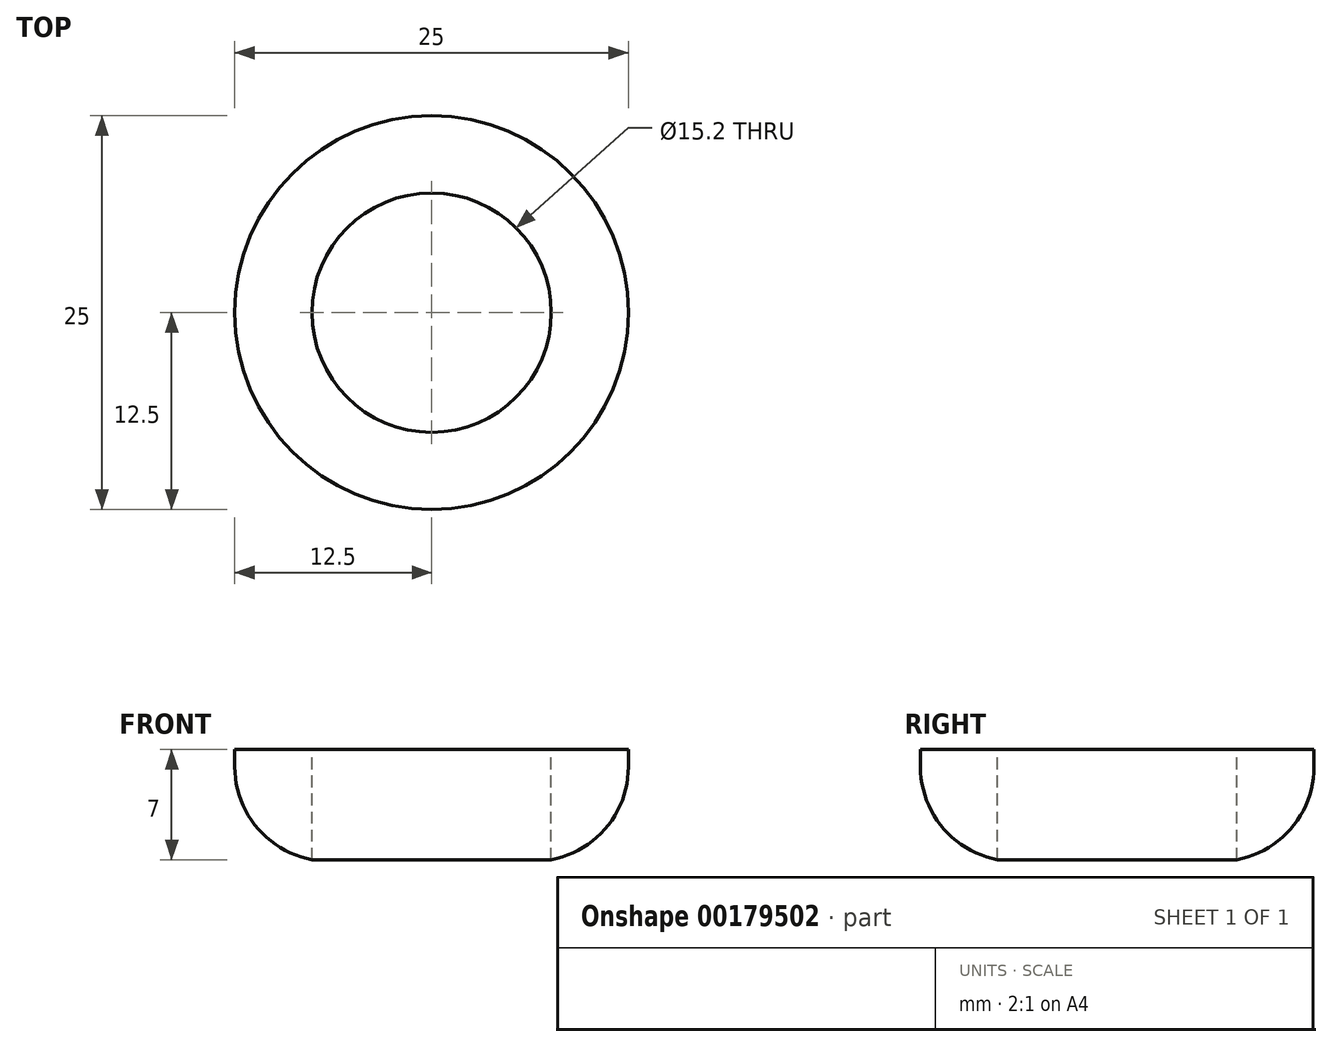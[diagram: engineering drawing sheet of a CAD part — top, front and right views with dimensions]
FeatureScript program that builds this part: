
annotation { "Feature Type Name" : "Feature", "Feature Type Description" : "" }
export const myFeature = defineFeature(function(context is Context, id is Id, definition is map)
    precondition{}
    {
        {
            var Q0;
            Q0=qCreatedBy(makeId("Top.planeOp"),FACE);
            var sketch = newSketch(context, id + "F0", { "sketchPlane" : qUnion([Q0])});
            skCircle(sketch, "E0", {"center": v(0, 0) * mm, "radius": 12.5 * mm});
            skCircle(sketch, "E1", {"center": v(0, 0) * mm, "radius": 7.6 * mm});
            skSolve(sketch);
        }
        {
            var Q0;
            Q0=qSketchRegion(id+"F0",true);
            extrude(context, id + "F1", {"entities" : qUnion([Q0]), "oppositeDirection" : true, "depth" : 7 * mm});
        }
        {
            var Q0;
            Q0=makeQuery(id+"F1.opExtrude","CAP_EDGE",EDGE,{"disambiguationData":[OSD([sQuery(id+"F0.wireOp",EDGE,"E0")])],"isStart":false});
            fillet(context, id + "F2", {"entities" : qUnion([Q0]), "radius" : 6 * mm, "tangentPropagation" : true, "allowEdgeOverflow" : false});
        }
    });
